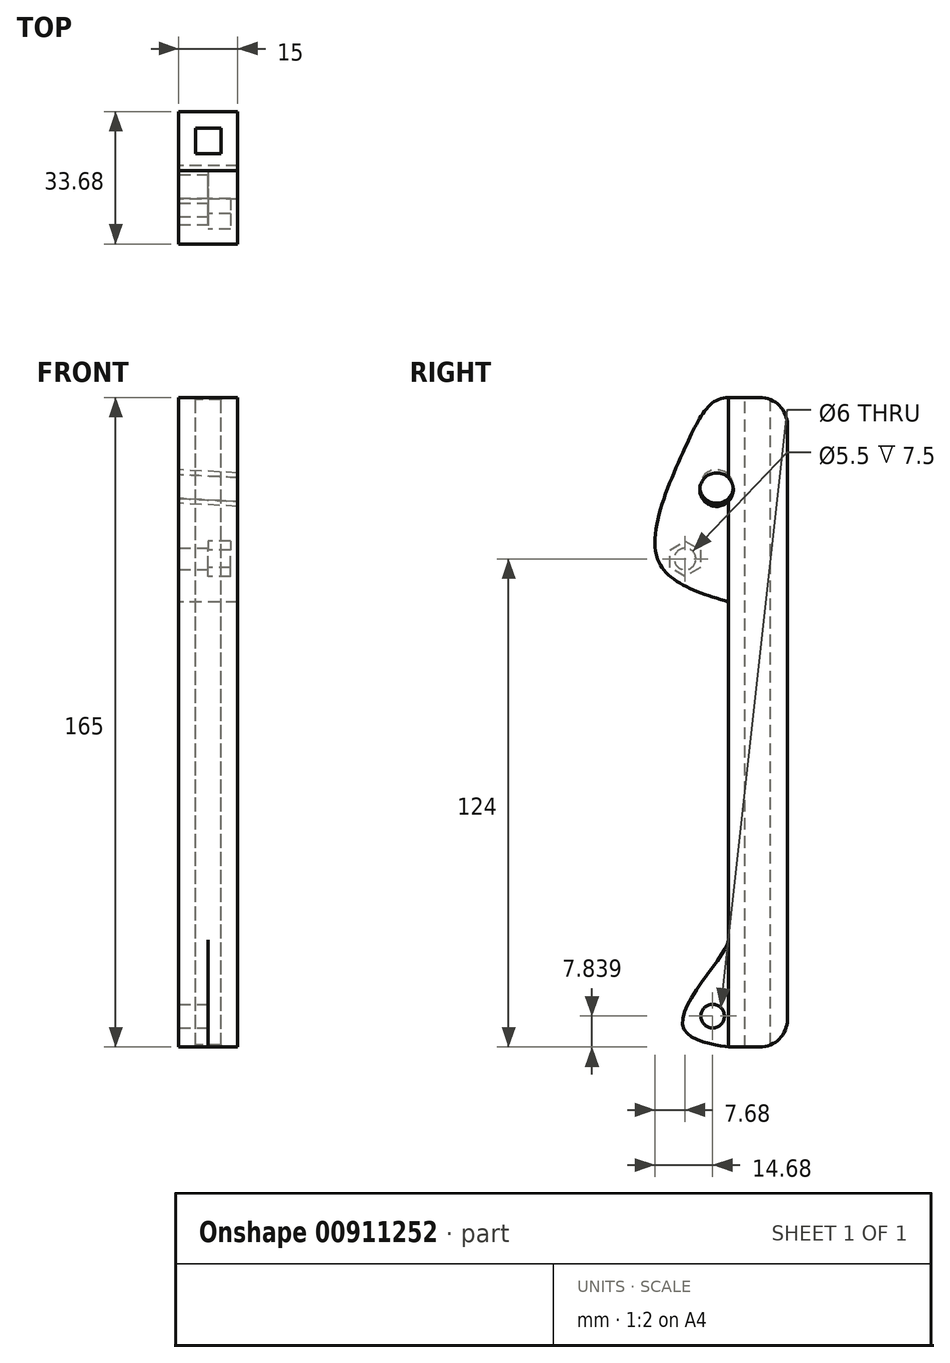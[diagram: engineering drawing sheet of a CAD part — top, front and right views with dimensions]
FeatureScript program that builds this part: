
annotation { "Feature Type Name" : "Feature", "Feature Type Description" : "" }
export const myFeature = defineFeature(function(context is Context, id is Id, definition is map)
    precondition{}
    {
        {
            var Q0;
            Q0=qCreatedBy(makeId("Right.planeOp"),FACE);
            var sketch = newSketch(context, id + "F0", { "sketchPlane" : qUnion([Q0])});
            skLineSegment(sketch, "E0.left", {"start": v(7.5, -95) * mm, "end": v(7.5, 70) * mm});
            skPoint(sketch, "E0.middle", {"position": v(0, 0) * mm});
            skLineSegment(sketch, "E1", {"start": v(7.5, 70) * mm, "end": v(-7.5, 70) * mm});
            skLineSegment(sketch, "E2", {"start": v(-7.5, 70) * mm, "end": v(-7.5, -95) * mm});
            skLineSegment(sketch, "E3", {"start": v(-7.5, -95) * mm, "end": v(7.5, -95) * mm});
            skSolve(sketch);
        }
        {
            var Q0;
            Q0=qSketchRegion(id+"F0",true);
            extrude(context, id + "F1", {"entities" : qUnion([Q0]), "endBound" : BoundingType.SYMMETRIC, "depth" : 15 * mm, "offsetDistance" : 25 * mm});
        }
        {
            var Q0;
            Q0=makeQuery(id+"F1.opExtrude","SWEPT_FACE",FACE,{"disambiguationData":[OSD([sQuery(id+"F0.wireOp",EDGE,"E1")])]});
            var sketch = newSketch(context, id + "F2", { "sketchPlane" : qUnion([Q0])});
            skLineSegment(sketch, "E4.bottom", {"start": v(3.25, 3.25) * mm, "end": v(-3.25, 3.25) * mm});
            skLineSegment(sketch, "E4.top", {"start": v(3.25, -3.25) * mm, "end": v(-3.25, -3.25) * mm});
            skLineSegment(sketch, "E4.left", {"start": v(3.25, 3.25) * mm, "end": v(3.25, -3.25) * mm});
            skLineSegment(sketch, "E4.right", {"start": v(-3.25, 3.25) * mm, "end": v(-3.25, -3.25) * mm});
            skPoint(sketch, "E4.middle", {"position": v(0, 0) * mm});
            skSolve(sketch);
        }
        {
            var Q0;
            Q0=qSketchRegion(id+"F2",true);
            extrude(context, id + "F3", {"entities" : qUnion([Q0]), "operationType" : NewBodyOperationType.REMOVE, "endBound" : BoundingType.THROUGH_ALL, "oppositeDirection" : true, "depth" : 25 * mm, "offsetDistance" : 25 * mm});
        }
        {
            var Q0;
            Q0=qCreatedBy(makeId("Right.planeOp"),FACE);
            var sketch = newSketch(context, id + "F4", { "sketchPlane" : qUnion([Q0])});
            skPoint(sketch, "E5", {"position": v(-10.5, 47) * mm});
            skSolve(sketch);
        }
        {
            var Q0;
            Q0=qCreatedBy(makeId("Right.planeOp"),FACE);
            var sketch = newSketch(context, id + "F5", { "sketchPlane" : qUnion([Q0])});
            skPoint(sketch, "E6", {"position": v(-18.5, 29) * mm});
            skPoint(sketch, "E7", {"position": v(-7.45, 18.07) * mm});
            skLineSegment(sketch, "E8", {"start": v(-18.5, 29) * mm, "end": v(-25.5, 29) * mm});
            skLineSegment(sketch, "E9", {"start": v(-18.5, 57.23) * mm, "end": v(-7.5, 57.23) * mm});
            skLineSegment(sketch, "E10", {"start": v(-7.45, 18.07) * mm, "end": v(-7.5, 57.23) * mm});
            skLineSegment(sketch, "E11.0", {"start": v(-18.5, 33.5) * mm, "end": v(-14.6, 31.25) * mm});
            skLineSegment(sketch, "E11.1", {"start": v(-14.6, 31.25) * mm, "end": v(-14.6, 26.75) * mm});
            skLineSegment(sketch, "E11.2", {"start": v(-14.6, 26.75) * mm, "end": v(-18.5, 24.5) * mm});
            skLineSegment(sketch, "E11.3", {"start": v(-18.5, 24.5) * mm, "end": v(-22.4, 26.75) * mm});
            skLineSegment(sketch, "E11.4", {"start": v(-22.4, 26.75) * mm, "end": v(-22.4, 31.25) * mm});
            skLineSegment(sketch, "E11.5", {"start": v(-22.4, 31.25) * mm, "end": v(-18.5, 33.5) * mm});
            skLineSegment(sketch, "E12", {"start": v(-7.5, 57.23) * mm, "end": v(-7.5, 70) * mm});
            skFitSpline(sketch, "E13", {"points": [v(-7.45, 18.07) * mm, v(-25.5, 29) * mm, v(-18.5, 57.23) * mm, v(-7.5, 70) * mm], "startDerivative": vector(-72.25, 21.38) * mm, "endDerivative": vector(53.85, 0.12) * mm});
            skSolve(sketch);
        }
        {
            var Q0;
            Q0=qSketchRegion(id+"F5",true);
            var Q1;
            Q1=makeQuery(id+"F5.imprint","IMPRINT",FACE,{"disambiguationData":[TD([[makeQuery(id+"F5.imprint","IMPRINT",EDGE,{"derivedFrom":sQuery(id+"F5.wireOp",EDGE,"E11.0")}),-1.0]])]});
            extrude(context, id + "F6", {"entities" : qUnion([Q0, Q1]), "endBound" : BoundingType.SYMMETRIC, "depth" : 15 * mm, "offsetDistance" : 25 * mm});
        }
        {
            var Q0;
            Q0=sQuery(id+"F5.wireOp",VERTEX,"E6");
            var Q1;
            Q1=makeQuery(id+"F6.opExtrude","SWEPT_BODY",BODY,{"disambiguationData":[OSD([sQuery(id+"F5.wireOp",EDGE,"d567c706-9595-4d48-b7f8-c94d3d51214e"),sQuery(id+"F5.wireOp",EDGE,"E9"),sQuery(id+"F5.wireOp",EDGE,"E10")])]});
            hole(context, id + "F7", {"style" : HoleStyle.SIMPLE, "endStyle" : HoleEndStyle.BLIND, "standardTappedOrClearance" : lookupTablePath({ "standard" : "ISO", "fit" : "Normal", "size" : "M5", "type" : "Clearance" }), "standardBlindInLast" : lookupTablePath({ "fit" : "Standard", "standard" : "ISO", "size" : "M5", "type" : "Clearance" }), "holeDiameter" : 5.5 * mm, "majorDiameter" : 5 * mm, "holeDepth" : 12 * mm, "isTappedThrough" : true, "tappedDepth" : 12 * mm, "tapClearance" : 3, "locations" : qUnion([Q0]), "scope" : qUnion([Q1])});
        }
        {
            var Q0;
            Q0=qCreatedBy(makeId("Right.planeOp"),FACE);
            var Q1;
            Q1=makeQuery(id+"F1.opExtrude","CAP_EDGE",EDGE,{"disambiguationData":[OSD([sQuery(id+"F0.wireOp",EDGE,"E1")])],"isStart":false});
            cPlane(context, id + "F8", {"entities" : qUnion([Q0, Q1]), "cplaneType" : CPlaneType.LINE_ANGLE, "offset" : 25 * mm, "angle" : 3 * degree, "oppositeDirection" : true, "width" : 150 * mm, "height" : 150 * mm});
        }
        {
            var Q0;
            Q0=qCreatedBy(id+"F8.planeOp",FACE);
            var sketch = newSketch(context, id + "F9", { "sketchPlane" : qUnion([Q0])});
            skCircle(sketch, "E14", {"center": v(10.5, 46.94) * mm, "radius": 4.25 * mm});
            skSolve(sketch);
        }
        {
            var Q0;
            Q0=qSketchRegion(id+"F9",true);
            extrude(context, id + "F10", {"entities" : qUnion([Q0]), "operationType" : NewBodyOperationType.REMOVE, "endBound" : BoundingType.SYMMETRIC, "oppositeDirection" : true, "depth" : 50 * mm, "offsetDistance" : 25 * mm});
        }
        {
            var Q0;
            Q0=qCreatedBy(makeId("Right.planeOp"),FACE);
            var sketch = newSketch(context, id + "F11", { "sketchPlane" : qUnion([Q0])});
            skPoint(sketch, "E15", {"position": v(-7.5, -95) * mm});
            skFitSpline(sketch, "E16", {"points": [v(-7.5, -95) * mm, v(-19.06, -89.77) * mm, v(-7.5, -67.81) * mm], "startDerivative": vector(-14.27, 3.2) * mm, "endDerivative": vector(-0.08, 18.34) * mm});
            skCircle(sketch, "E17", {"center": v(-11.5, -87.16) * mm, "radius": 3 * mm});
            skLineSegment(sketch, "E18", {"start": v(-7.5, -67.81) * mm, "end": v(-7.5, -95) * mm});
            skSolve(sketch);
        }
        {
            var Q0;
            Q0=qSketchRegion(id+"F11",true);
            extrude(context, id + "F12", {"entities" : qUnion([Q0]), "operationType" : NewBodyOperationType.ADD, "oppositeDirection" : true, "depth" : 7.5 * mm, "offsetDistance" : 25 * mm});
        }
        {
            var Q0;
            Q0=makeQuery(id+"F5.imprint","IMPRINT",FACE,{"disambiguationData":[TD([[makeQuery(id+"F5.imprint","IMPRINT",EDGE,{"derivedFrom":sQuery(id+"F5.wireOp",EDGE,"E11.0")}),-1.0]])]});
            extrude(context, id + "F13", {"entities" : qUnion([Q0]), "operationType" : NewBodyOperationType.REMOVE, "depth" : 5.7 * mm, "offsetDistance" : 25 * mm});
        }
        {
            var Q0;
            Q0=makeQuery(id+"F1.opExtrude","SWEPT_EDGE",EDGE,{"disambiguationData":[OSD([sQuery(id+"F0.wireOp",EDGE,"E0.left"),sQuery(id+"F0.wireOp",EDGE,"E1")])]});
            var Q1;
            Q1=makeQuery(id+"F1.opExtrude","SWEPT_EDGE",EDGE,{"disambiguationData":[OSD([sQuery(id+"F0.wireOp",EDGE,"E0.left"),sQuery(id+"F0.wireOp",EDGE,"E3")])]});
            fillet(context, id + "F14", {"entities" : qUnion([Q0, Q1]), "radius" : 7 * mm, "tangentPropagation" : true, "allowEdgeOverflow" : false});
        }
    });
